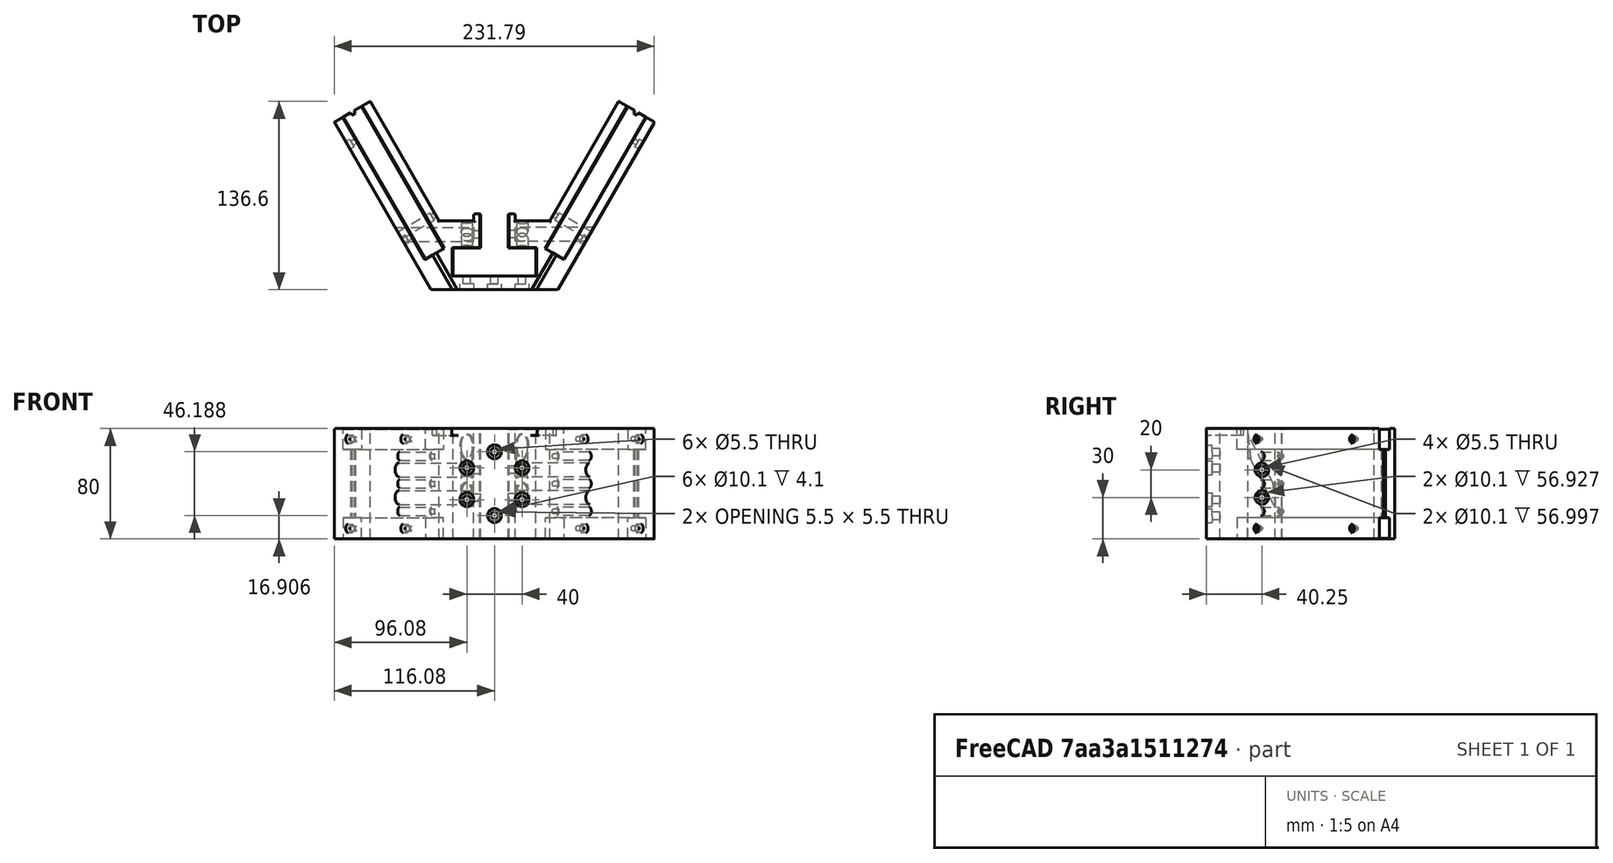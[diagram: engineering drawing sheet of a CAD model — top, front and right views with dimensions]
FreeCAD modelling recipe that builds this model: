
FCSTD DOCUMENT  (FreeCAD 2022.430R26244 +4758 (Git))
Label: as3bottom_corner-M3x10
License: All rights reserved
LicenseURL: http://en.wikipedia.org/wiki/All_rights_reserved
objects: Part::FeaturePython×13, App::FeaturePython×2, Part::Feature×1
note: 13 computed .brp shape members not serialized (recipe doc carries the construction recipe); baked Part::Feature solids carry a one-line shape summary decoded from their .brp

FEATURE [App::FeaturePython] Constraints  # WARN: FeaturePython — macro-defined, semantics opaque (R4)
  TreeRank = 0
  _LinkVersion = 1
  _Version = 1
FEATURE [Part::Feature] ShapeCopy  label="BottomCornerM3x10"
  TreeRank = 44
  shape: bbox 232.2 x 136.6 x 80 mm, 177 faces (baked)
FEATURE [Part::FeaturePython] Parts  # WARN: FeaturePython — macro-defined, semantics opaque (R4)
  Group = -> [ShapeCopy]
  GroupMode = 0
  TreeRank = 0
  _LinkVersion = 1
FEATURE [Part::FeaturePython] Assembly  label="As3BottomCorner-M3x10"  # WARN: FeaturePython — macro-defined, semantics opaque (R4)
  AutoRelax = true
  BuildShape = 0
  Freeze = false
  Group = -> [Constraints,Elements,Parts]
  TreeRank = 0
  Verbose = false
  _LinkVersion = 1
  _SolverType = 1
  _Version = 1
FEATURE [App::FeaturePython] Elements  # WARN: FeaturePython — macro-defined, semantics opaque (R4)
  Group = -> [Element,Element001,Element002,Element003,Element004,Element005,Element006,Element007,Element008,Element009,Element010]
  TreeRank = 0
  _LinkVersion = 1
FEATURE [Part::FeaturePython] Element  label="FaceRef"  # link proxy (typed FeaturePython)
  Detach = false
  LinkTransform = true
  LinkedObject = -> ShapeCopy [Face37]
  TreeRank = 0
  _LinkVersion = 1
  _Parent = -> Elements
FEATURE [Part::FeaturePython] Element001  label="AppuiPoteau1"  # link proxy (typed FeaturePython)
  Detach = false
  LinkTransform = true
  LinkedObject = -> ShapeCopy [Face9]
  TreeRank = 0
  _LinkVersion = 1
  _Parent = -> Elements
FEATURE [Part::FeaturePython] Element002  label="AppuiPoteau2"  # link proxy (typed FeaturePython)
  Detach = false
  LinkTransform = true
  LinkedObject = -> ShapeCopy [Face35]
  TreeRank = 0
  _LinkVersion = 1
  _Parent = -> Elements
FEATURE [Part::FeaturePython] Element003  label="AppuiTrav1v"  # link proxy (typed FeaturePython)
  Detach = false
  LinkTransform = true
  LinkedObject = -> ShapeCopy [Face51]
  TreeRank = 0
  _LinkVersion = 1
  _Parent = -> Elements
FEATURE [Part::FeaturePython] Element004  label="AppuiTrav1h"  # link proxy (typed FeaturePython)
  Detach = false
  LinkTransform = true
  LinkedObject = -> ShapeCopy [Face49]
  TreeRank = 0
  _LinkVersion = 1
  _Parent = -> Elements
FEATURE [Part::FeaturePython] Element005  label="AppuiTrav2h"  # link proxy (typed FeaturePython)
  Detach = false
  LinkTransform = true
  LinkedObject = -> ShapeCopy [Face45]
  TreeRank = 0
  _LinkVersion = 1
  _Parent = -> Elements
FEATURE [Part::FeaturePython] Element006  label="AppuiTrv2v"  # link proxy (typed FeaturePython)
  Detach = false
  LinkTransform = true
  LinkedObject = -> ShapeCopy [Face79]
  TreeRank = 0
  _LinkVersion = 1
  _Parent = -> Elements
FEATURE [Part::FeaturePython] Element007  label="ExtremRain1"  # link proxy (typed FeaturePython)
  Detach = false
  LinkTransform = true
  LinkedObject = -> ShapeCopy [Face12]
  TreeRank = 0
  _LinkVersion = 1
  _Parent = -> Elements
FEATURE [Part::FeaturePython] Element008  label="ExtremRain2"  # link proxy (typed FeaturePython)
  Detach = false
  LinkTransform = true
  LinkedObject = -> ShapeCopy [Face25]
  TreeRank = 0
  _LinkVersion = 1
  _Parent = -> Elements
FEATURE [Part::FeaturePython] Element009  label="FixM1"  # link proxy (typed FeaturePython)
  Detach = false
  LinkTransform = true
  LinkedObject = -> ShapeCopy [Edge168]
  TreeRank = 0
  _LinkVersion = 1
  _Parent = -> Elements
FEATURE [Part::FeaturePython] Element010  label="FixM2"  # link proxy (typed FeaturePython)
  Detach = false
  LinkTransform = true
  LinkedObject = -> ShapeCopy [Edge287]
  TreeRank = 0
  _LinkVersion = 1
  _Parent = -> Elements
